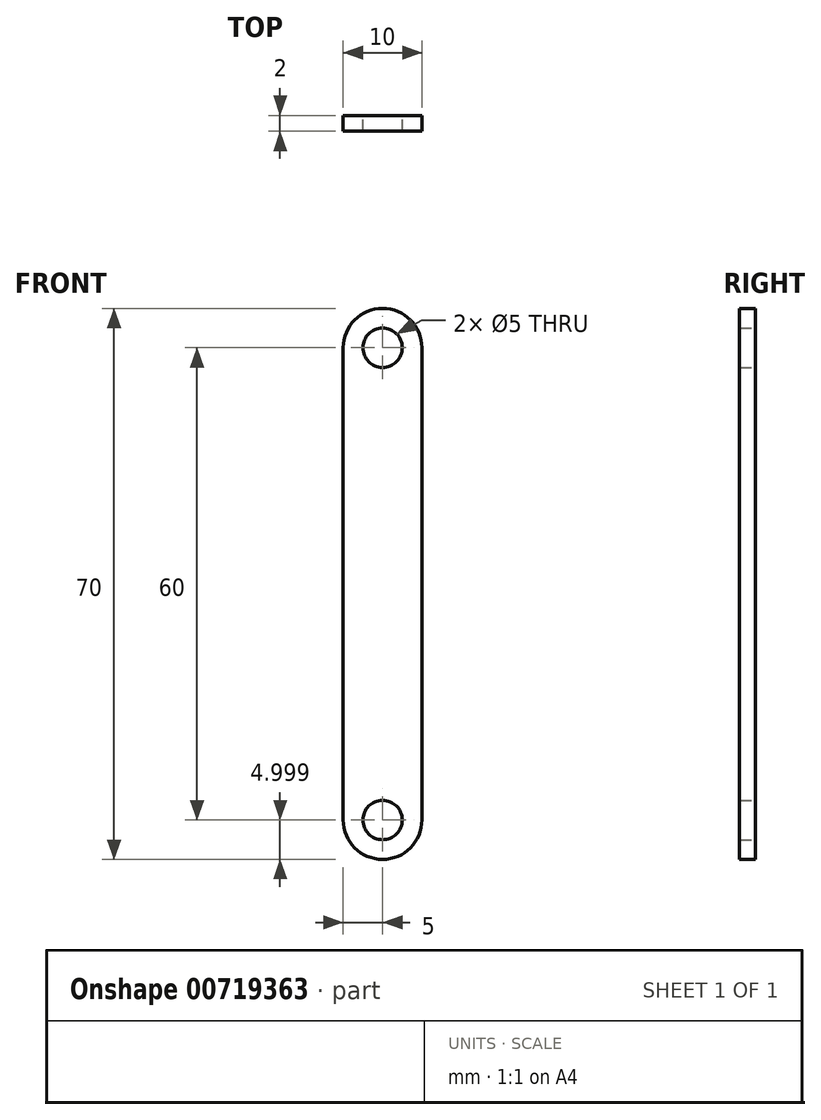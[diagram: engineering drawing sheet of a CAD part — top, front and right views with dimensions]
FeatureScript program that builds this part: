
annotation { "Feature Type Name" : "Feature", "Feature Type Description" : "" }
export const myFeature = defineFeature(function(context is Context, id is Id, definition is map)
    precondition{}
    {
        {
            var Q0;
            Q0=qCreatedBy(makeId("Front.planeOp"),FACE);
            var sketch = newSketch(context, id + "F0", { "sketchPlane" : qUnion([Q0])});
            skLineSegment(sketch, "E0.bottom", {"start": v(33.12, 90.95) * mm, "end": v(33.12, 90.95) * mm});
            skLineSegment(sketch, "E0.top", {"start": v(33.12, 20.95) * mm, "end": v(33.12, 20.95) * mm});
            skLineSegment(sketch, "E0.left", {"start": v(28.12, 85.95) * mm, "end": v(28.12, 25.95) * mm});
            skLineSegment(sketch, "E0.right", {"start": v(38.12, 85.95) * mm, "end": v(38.12, 25.95) * mm});
            skPoint(sketch, "E1.visualSharp", {"position": v(28.12, 90.95) * mm});
            skArc(sketch, "E1.filletArc", {"start": v(33.12, 90.95) * mm, "mid": v(29.58, 89.48) * mm, "end": v(28.12, 85.95) * mm});
            skPoint(sketch, "E2.visualSharp", {"position": v(38.12, 90.95) * mm});
            skArc(sketch, "E2.filletArc", {"start": v(38.12, 85.95) * mm, "mid": v(36.66, 89.48) * mm, "end": v(33.12, 90.95) * mm});
            skPoint(sketch, "E3.visualSharp", {"position": v(28.12, 20.95) * mm});
            skArc(sketch, "E3.filletArc", {"start": v(28.12, 25.95) * mm, "mid": v(29.58, 22.41) * mm, "end": v(33.12, 20.95) * mm});
            skPoint(sketch, "E4.visualSharp", {"position": v(38.12, 20.95) * mm});
            skArc(sketch, "E4.filletArc", {"start": v(33.12, 20.95) * mm, "mid": v(36.66, 22.41) * mm, "end": v(38.12, 25.95) * mm});
            skCircle(sketch, "E5", {"center": v(33.12, 85.95) * mm, "radius": 2.5 * mm});
            skCircle(sketch, "E6", {"center": v(33.12, 25.95) * mm, "radius": 2.5 * mm});
            skSolve(sketch);
        }
        {
            var Q0;
            Q0 = qSketchRegion(id + "F0", true);
            extrude(context, id + "F1", {"entities" : qUnion([Q0]), "depth" : 2 * mm, "offsetDistance" : 25.4 * mm});
        }
    });
